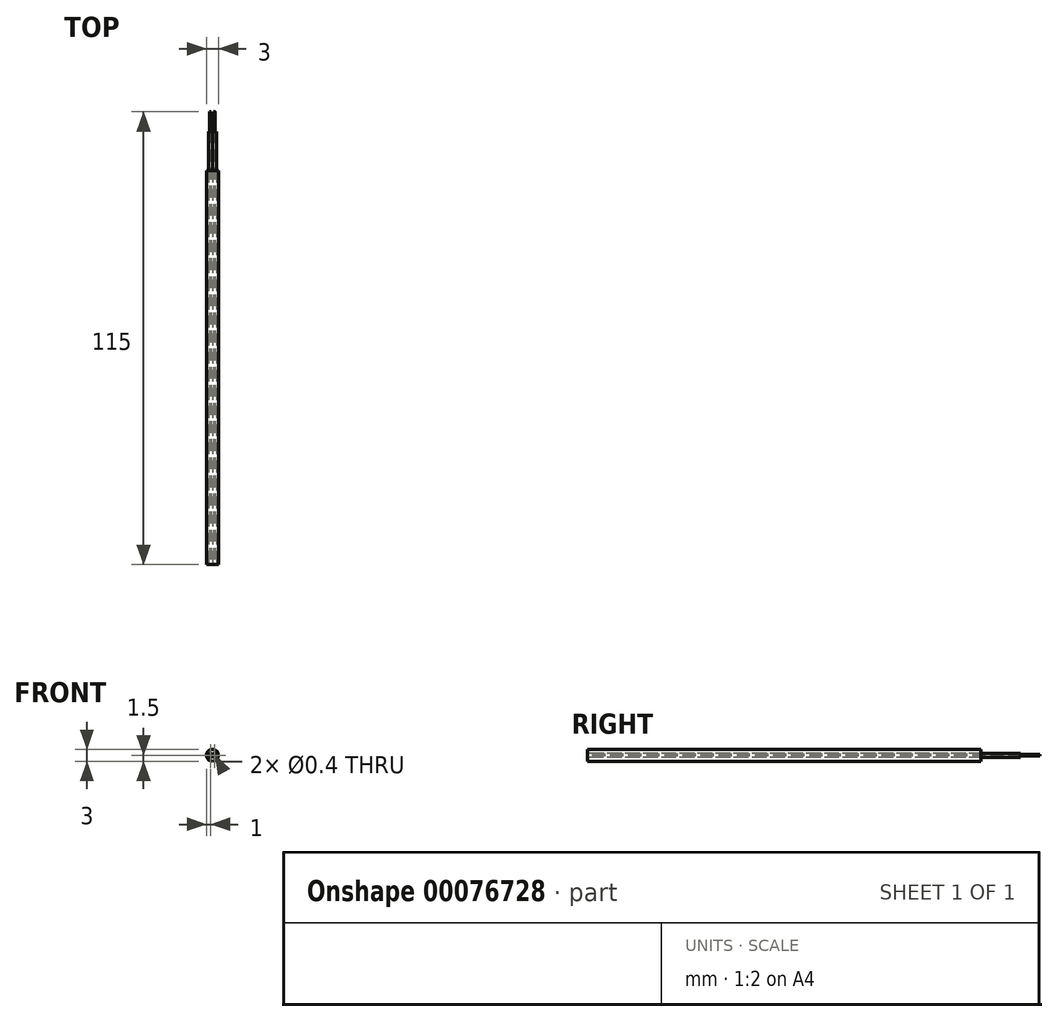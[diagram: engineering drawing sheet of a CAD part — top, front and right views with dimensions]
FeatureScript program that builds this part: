
annotation { "Feature Type Name" : "Feature", "Feature Type Description" : "" }
export const myFeature = defineFeature(function(context is Context, id is Id, definition is map)
    precondition{}
    {
        {
            var Q0;
            Q0=qCreatedBy(makeId("Front.planeOp"),FACE);
            var sketch = newSketch(context, id + "F0", { "sketchPlane" : qUnion([Q0])});
            skCircle(sketch, "E0", {"center": v(0, 0) * mm, "radius": 1.5 * mm});
            skSolve(sketch);
        }
        {
            var Q0;
            Q0=makeQuery(id+"F0.imprint","IMPRINT",FACE,{"disambiguationData":[TD([[makeQuery(id+"F0.imprint","IMPRINT",EDGE,{"derivedFrom":sQuery(id+"F0.wireOp",EDGE,"E0")}),1.0]])]});
            extrude(context, id + "F1", {"entities" : qUnion([Q0]), "depth" : 100 * mm, "symmetric" : true});
        }
        {
            var Q0;
            Q0=makeQuery(id+"F1.opExtrude","CAP_FACE",FACE,{"disambiguationData":[OSD([sQuery(id+"F0.wireOp",EDGE,"E0")])],"isStart":false});
            var sketch = newSketch(context, id + "F2", { "sketchPlane" : qUnion([Q0])});
            skLineSegment(sketch, "E1", {"start": v(0, 1.71) * mm, "end": v(0, -1.74) * mm, "construction": true});
            skCircle(sketch, "E2", {"center": v(0.5, 0) * mm, "radius": 0.5 * mm});
            skCircle(sketch, "E3", {"center": v(-0.5, 0) * mm, "radius": 0.5 * mm});
            skCircle(sketch, "E4", {"center": v(-0.5, 0) * mm, "radius": 0.2 * mm});
            skCircle(sketch, "E5", {"center": v(0.5, 0) * mm, "radius": 0.2 * mm});
            skSolve(sketch);
        }
        {
            var Q0;
            Q0=makeQuery(id+"F2.imprint","IMPRINT",FACE,{"disambiguationData":[TD([[makeQuery(id+"F2.imprint","IMPRINT",EDGE,{"derivedFrom":sQuery(id+"F2.wireOp",EDGE,"E2")}),1.0]])]});
            extrude(context, id + "F3", {"entities" : qUnion([Q0]), "oppositeDirection" : true, "depth" : 110 * mm});
        }
        {
            var Q0;
            Q0=makeQuery(id+"F2.imprint","IMPRINT",FACE,{"disambiguationData":[TD([[makeQuery(id+"F2.imprint","IMPRINT",EDGE,{"derivedFrom":sQuery(id+"F2.wireOp",EDGE,"E3")}),1.0]])]});
            extrude(context, id + "F4", {"entities" : qUnion([Q0]), "oppositeDirection" : true, "depth" : 110 * mm});
        }
        {
            var Q0;
            Q0=makeQuery(id+"F2.imprint","IMPRINT",FACE,{"disambiguationData":[TD([[makeQuery(id+"F2.imprint","IMPRINT",EDGE,{"derivedFrom":sQuery(id+"F2.wireOp",EDGE,"E4")}),1.0]])]});
            var Q1;
            Q1=makeQuery(id+"F2.imprint","IMPRINT",FACE,{"disambiguationData":[TD([[makeQuery(id+"F2.imprint","IMPRINT",EDGE,{"derivedFrom":sQuery(id+"F2.wireOp",EDGE,"E5")}),1.0]])]});
            extrude(context, id + "F5", {"entities" : qUnion([Q0, Q1]), "oppositeDirection" : true, "depth" : 115 * mm});
        }
    });
